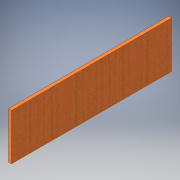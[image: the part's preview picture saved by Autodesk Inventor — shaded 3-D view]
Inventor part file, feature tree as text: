
AUTODESK INVENTOR PART (.ipt)
format: ipt  version: 2016 (Build 200138000, 138)  size: 102,400 bytes
history: native  units: in
note: dims shown in document units (in); Inventor stores cm internally (conversion verified against a paired STEP export)
features: extrude x1, sketch x1
ambient origin geometry x8: Origin, YZ Plane, XZ Plane, XY Plane, X Axis, Y Axis, Z Axis, Center Point
bodies: Solid1 (feature_tree)
feature tree (2):
  extrude  "Extrusion1"  Depth=6.5in
  sketch  "Sketch1"  dims[d0=22.5in d1=6.5in d2=0.4375in d3=0.0in]
